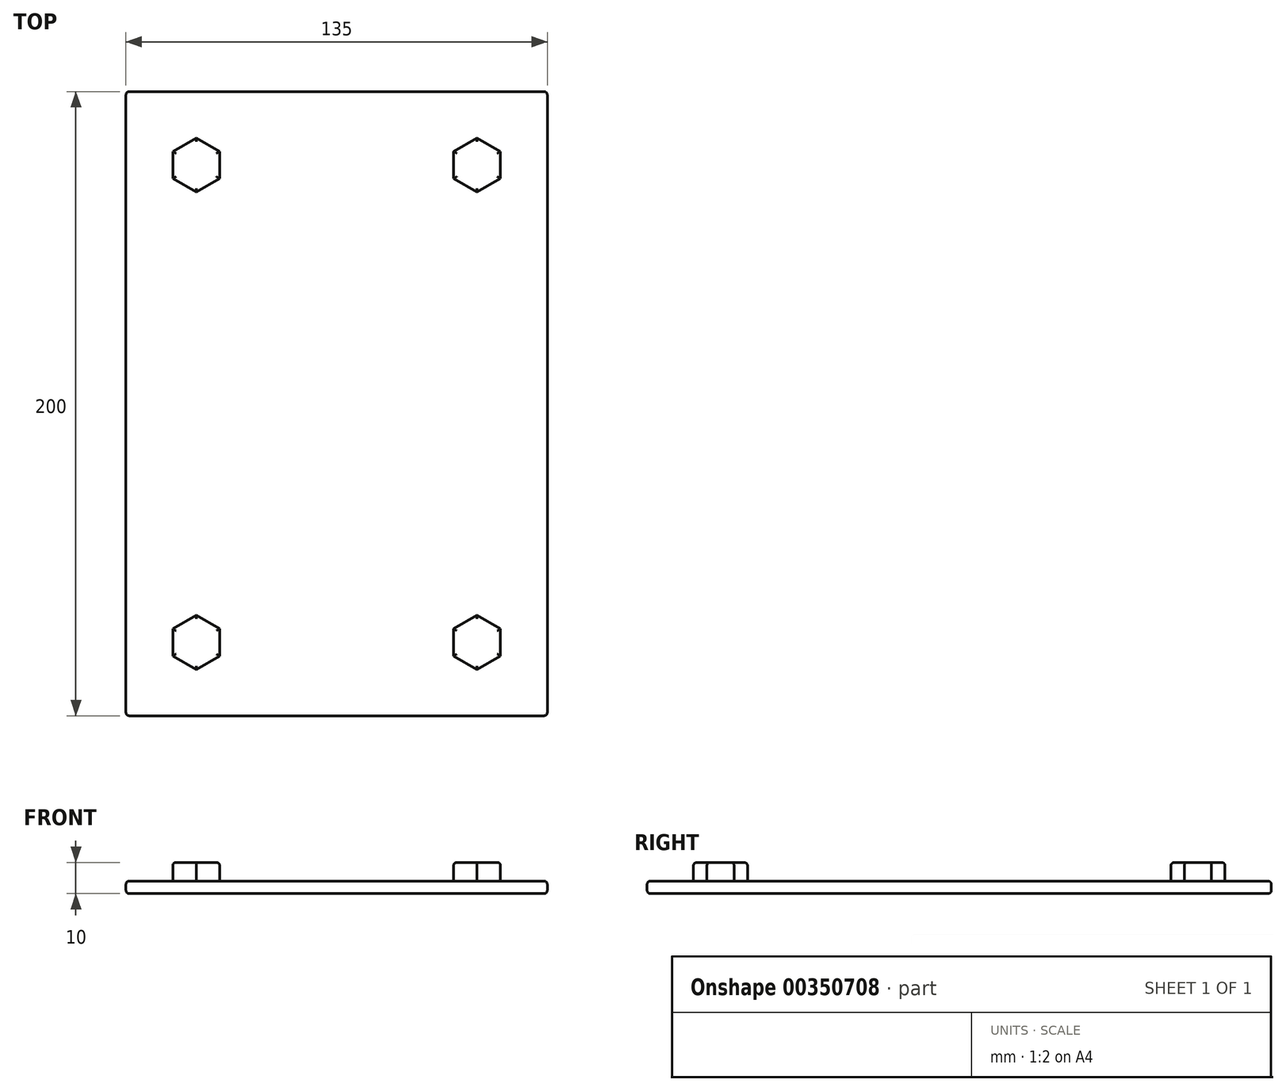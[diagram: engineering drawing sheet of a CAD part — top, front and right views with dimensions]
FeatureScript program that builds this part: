
annotation { "Feature Type Name" : "Feature", "Feature Type Description" : "" }
export const myFeature = defineFeature(function(context is Context, id is Id, definition is map)
    precondition{}
    {
        {
            var Q0;
            Q0=qCreatedBy(makeId("Top.planeOp"),FACE);
            var sketch = newSketch(context, id + "F0", { "sketchPlane" : qUnion([Q0])});
            skLineSegment(sketch, "E0", {"start": v(0, 0) * mm, "end": v(0, 200) * mm});
            skLineSegment(sketch, "E1", {"start": v(0, 200) * mm, "end": v(135, 200) * mm});
            skLineSegment(sketch, "E2", {"start": v(135, 200) * mm, "end": v(135, 0) * mm});
            skLineSegment(sketch, "E3", {"start": v(135, 0) * mm, "end": v(0, 0) * mm});
            skSolve(sketch);
        }
        {
            var Q0;
            Q0=qSketchRegion(id+"F0",true);
            extrude(context, id + "F1", {"entities" : qUnion([Q0]), "depth" : 4 * mm});
        }
        {
            var Q0;
            Q0=makeQuery(id+"F1.opExtrude","CAP_FACE",FACE,{"disambiguationData":[OSD([sQuery(id+"F0.wireOp",EDGE,"E0"),sQuery(id+"F0.wireOp",EDGE,"E1"),sQuery(id+"F0.wireOp",EDGE,"E2"),sQuery(id+"F0.wireOp",EDGE,"E3")])],"isStart":false});
            var Q1;
            Q1=makeQuery(id+"F1.opExtrude","CAP_FACE",FACE,{"disambiguationData":[OSD([sQuery(id+"F0.wireOp",EDGE,"E0"),sQuery(id+"F0.wireOp",EDGE,"E1"),sQuery(id+"F0.wireOp",EDGE,"E2"),sQuery(id+"F0.wireOp",EDGE,"E3")])],"isStart":true});
            var Q2;
            Q2=makeQuery(id+"F1.opExtrude","SWEPT_EDGE",EDGE,{"disambiguationData":[OSD([sQuery(id+"F0.wireOp",EDGE,"E2"),sQuery(id+"F0.wireOp",EDGE,"E3")])]});
            var Q3;
            Q3=makeQuery(id+"F1.opExtrude","SWEPT_EDGE",EDGE,{"disambiguationData":[OSD([sQuery(id+"F0.wireOp",EDGE,"E0"),sQuery(id+"F0.wireOp",EDGE,"E3")])]});
            var Q4;
            Q4=makeQuery(id+"F1.opExtrude","SWEPT_EDGE",EDGE,{"disambiguationData":[OSD([sQuery(id+"F0.wireOp",EDGE,"E1"),sQuery(id+"F0.wireOp",EDGE,"E2")])]});
            var Q5;
            Q5=makeQuery(id+"F1.opExtrude","SWEPT_EDGE",EDGE,{"disambiguationData":[OSD([sQuery(id+"F0.wireOp",EDGE,"E0"),sQuery(id+"F0.wireOp",EDGE,"E1")])]});
            fillet(context, id + "F2", {"entities" : qUnion([Q0, Q1, Q2, Q3, Q4, Q5]), "radius" : 1 * mm, "tangentPropagation" : true, "allowEdgeOverflow" : false});
        }
        {
            var Q0;
            Q0=makeQuery(id+"F1.opExtrude","CAP_FACE",FACE,{"disambiguationData":[OSD([sQuery(id+"F0.wireOp",EDGE,"E0"),sQuery(id+"F0.wireOp",EDGE,"E1"),sQuery(id+"F0.wireOp",EDGE,"E2"),sQuery(id+"F0.wireOp",EDGE,"E3")])],"isStart":false});
            var sketch = newSketch(context, id + "F3", { "sketchPlane" : qUnion([Q0])});
            skCircle(sketch, "E4.cCircle", {"center": v(22.5, 176.5) * mm, "radius": 7.5 * mm, "construction": true});
            skLineSegment(sketch, "E4.0", {"start": v(30, 172.17) * mm, "end": v(22.5, 167.84) * mm});
            skLineSegment(sketch, "E4.1", {"start": v(22.5, 167.84) * mm, "end": v(15, 172.17) * mm});
            skLineSegment(sketch, "E4.2", {"start": v(15, 172.17) * mm, "end": v(15, 180.83) * mm});
            skLineSegment(sketch, "E4.3", {"start": v(15, 180.83) * mm, "end": v(22.5, 185.16) * mm});
            skLineSegment(sketch, "E4.4", {"start": v(22.5, 185.16) * mm, "end": v(30, 180.83) * mm});
            skLineSegment(sketch, "E4.5", {"start": v(30, 180.83) * mm, "end": v(30, 172.17) * mm});
            skPoint(sketch, "E4.0.midPoint", {"position": v(26.25, 170) * mm});
            skLineSegment(sketch, "E5", {"start": v(67.5, 199) * mm, "end": v(67.5, 1) * mm, "construction": true});
            skLineSegment(sketch, "E6", {"start": v(1, 100) * mm, "end": v(134, 100) * mm, "construction": true});
            skLineSegment(sketch, "E7.MirrorCS", {"start": v(112.5, 185.16) * mm, "end": v(105, 180.83) * mm});
            skLineSegment(sketch, "E8.MirrorCS", {"start": v(120, 180.83) * mm, "end": v(112.5, 185.16) * mm});
            skLineSegment(sketch, "E9.MirrorCS", {"start": v(120, 172.17) * mm, "end": v(120, 180.83) * mm});
            skLineSegment(sketch, "E10.MirrorCS", {"start": v(112.5, 167.84) * mm, "end": v(120, 172.17) * mm});
            skLineSegment(sketch, "E11.MirrorCS", {"start": v(105, 180.83) * mm, "end": v(105, 172.17) * mm});
            skLineSegment(sketch, "E12.MirrorCS", {"start": v(105, 172.17) * mm, "end": v(112.5, 167.84) * mm});
            skPoint(sketch, "E13.MirrorP", {"position": v(108.75, 170) * mm});
            skCircle(sketch, "E14.MirrorC", {"center": v(112.5, 176.5) * mm, "radius": 7.5 * mm, "construction": true});
            skLineSegment(sketch, "E15.MirrorCS", {"start": v(134, 100) * mm, "end": v(1, 100) * mm, "construction": true});
            skLineSegment(sketch, "E16.MirrorCS", {"start": v(30, 27.83) * mm, "end": v(22.5, 32.16) * mm});
            skLineSegment(sketch, "E17.MirrorCS", {"start": v(15, 19.17) * mm, "end": v(22.5, 14.84) * mm});
            skLineSegment(sketch, "E18.MirrorCS", {"start": v(22.5, 32.16) * mm, "end": v(15, 27.83) * mm});
            skLineSegment(sketch, "E19.MirrorCS", {"start": v(15, 27.83) * mm, "end": v(15, 19.17) * mm});
            skLineSegment(sketch, "E20.MirrorCS", {"start": v(22.5, 14.84) * mm, "end": v(30, 19.17) * mm});
            skPoint(sketch, "E21.MirrorP", {"position": v(26.25, 30) * mm});
            skCircle(sketch, "E22.MirrorC", {"center": v(22.5, 23.5) * mm, "radius": 7.5 * mm, "construction": true});
            skLineSegment(sketch, "E23.MirrorCS", {"start": v(30, 19.17) * mm, "end": v(30, 27.83) * mm});
            skLineSegment(sketch, "E24.MirrorCS", {"start": v(112.5, 14.84) * mm, "end": v(105, 19.17) * mm});
            skLineSegment(sketch, "E25.MirrorCS", {"start": v(105, 27.83) * mm, "end": v(112.5, 32.16) * mm});
            skLineSegment(sketch, "E26.MirrorCS", {"start": v(120, 27.83) * mm, "end": v(120, 19.17) * mm});
            skLineSegment(sketch, "E27.MirrorCS", {"start": v(112.5, 32.16) * mm, "end": v(120, 27.83) * mm});
            skLineSegment(sketch, "E28.MirrorCS", {"start": v(120, 19.17) * mm, "end": v(112.5, 14.84) * mm});
            skPoint(sketch, "E29.MirrorP", {"position": v(108.75, 30) * mm});
            skLineSegment(sketch, "E30.MirrorCS", {"start": v(105, 19.17) * mm, "end": v(105, 27.83) * mm});
            skCircle(sketch, "E31.MirrorC", {"center": v(112.5, 23.5) * mm, "radius": 7.5 * mm, "construction": true});
            skSolve(sketch);
        }
        {
            var Q0;
            Q0=qSketchRegion(id+"F3",true);
            extrude(context, id + "F4", {"entities" : qUnion([Q0]), "operationType" : NewBodyOperationType.ADD, "depth" : 6 * mm});
        }
        {
            var Q0;
            Q0=makeQuery(id+"F4.opExtrude","CAP_FACE",FACE,{"disambiguationData":[OSD([sQuery(id+"F3.wireOp",EDGE,"E4.1"),sQuery(id+"F3.wireOp",EDGE,"E4.0"),sQuery(id+"F3.wireOp",EDGE,"E4.5"),sQuery(id+"F3.wireOp",EDGE,"E4.2"),sQuery(id+"F3.wireOp",EDGE,"E4.4"),sQuery(id+"F3.wireOp",EDGE,"E4.3")])],"isStart":false});
            var Q1;
            Q1=makeQuery(id+"F4.opExtrude","CAP_FACE",FACE,{"disambiguationData":[OSD([sQuery(id+"F3.wireOp",EDGE,"E12.MirrorCS"),sQuery(id+"F3.wireOp",EDGE,"E10.MirrorCS"),sQuery(id+"F3.wireOp",EDGE,"E11.MirrorCS"),sQuery(id+"F3.wireOp",EDGE,"E7.MirrorCS"),sQuery(id+"F3.wireOp",EDGE,"E9.MirrorCS"),sQuery(id+"F3.wireOp",EDGE,"E8.MirrorCS")])],"isStart":false});
            var Q2;
            Q2=makeQuery(id+"F4.opExtrude","CAP_FACE",FACE,{"disambiguationData":[OSD([sQuery(id+"F3.wireOp",EDGE,"E27.MirrorCS"),sQuery(id+"F3.wireOp",EDGE,"E26.MirrorCS"),sQuery(id+"F3.wireOp",EDGE,"E24.MirrorCS"),sQuery(id+"F3.wireOp",EDGE,"E28.MirrorCS"),sQuery(id+"F3.wireOp",EDGE,"E25.MirrorCS"),sQuery(id+"F3.wireOp",EDGE,"E30.MirrorCS")])],"isStart":false});
            var Q3;
            Q3=makeQuery(id+"F4.opExtrude","CAP_FACE",FACE,{"disambiguationData":[OSD([sQuery(id+"F3.wireOp",EDGE,"E16.MirrorCS"),sQuery(id+"F3.wireOp",EDGE,"E17.MirrorCS"),sQuery(id+"F3.wireOp",EDGE,"E18.MirrorCS"),sQuery(id+"F3.wireOp",EDGE,"E23.MirrorCS"),sQuery(id+"F3.wireOp",EDGE,"E20.MirrorCS"),sQuery(id+"F3.wireOp",EDGE,"E19.MirrorCS")])],"isStart":false});
            fillet(context, id + "F5", {"entities" : qUnion([Q0, Q1, Q2, Q3]), "radius" : 1 * mm, "tangentPropagation" : true, "allowEdgeOverflow" : false});
        }
    });
